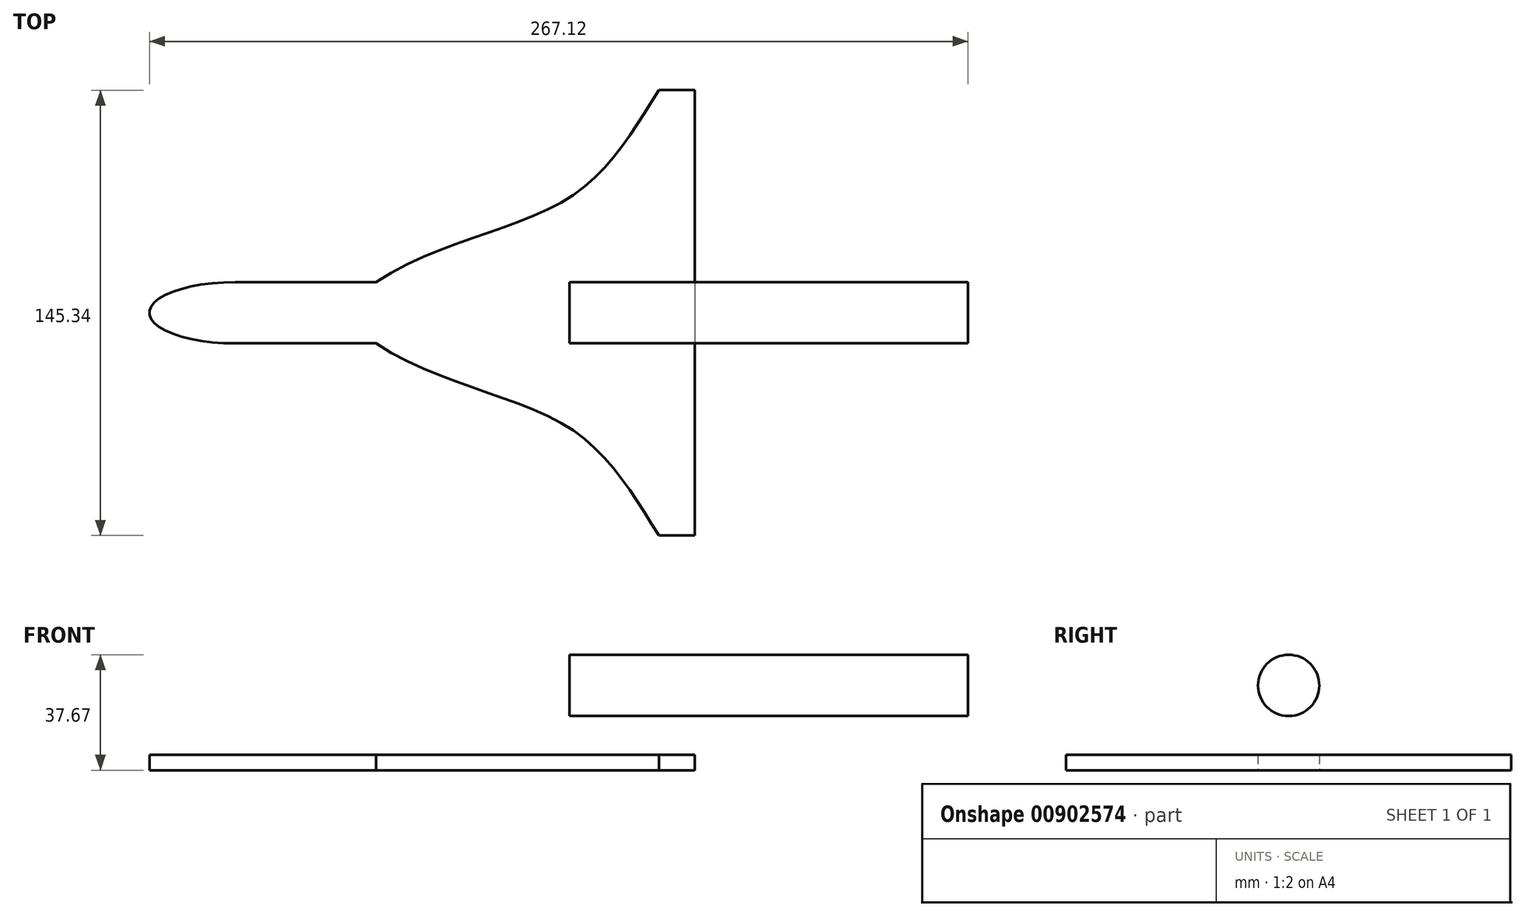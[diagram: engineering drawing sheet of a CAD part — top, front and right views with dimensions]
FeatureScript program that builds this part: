
annotation { "Feature Type Name" : "Feature", "Feature Type Description" : "" }
export const myFeature = defineFeature(function(context is Context, id is Id, definition is map)
    precondition{}
    {
        {
            var Q0;
            Q0=qCreatedBy(makeId("Top.planeOp"),FACE);
            var sketch = newSketch(context, id + "F0", { "sketchPlane" : qUnion([Q0])});
            skLineSegment(sketch, "E0", {"start": v(-109.12, 10) * mm, "end": v(40.88, 10) * mm});
            skLineSegment(sketch, "E1", {"start": v(40.88, 10) * mm, "end": v(40.88, 0) * mm});
            skLineSegment(sketch, "E2.MirrorCS", {"start": v(-109.12, -10) * mm, "end": v(40.88, -10) * mm});
            skLineSegment(sketch, "E3.MirrorCS", {"start": v(40.88, -10) * mm, "end": v(40.88, 0) * mm});
            skFitSpline(sketch, "E4", {"points": [v(-63.22, 10) * mm, v(0, 37.65) * mm, v(29.12, 72.67) * mm], "startDerivative": vector(113.66, 74.72) * mm, "endDerivative": vector(53.85, 84.54) * mm});
            skLineSegment(sketch, "E5", {"start": v(29.12, 72.67) * mm, "end": v(46, 72.67) * mm});
            skLineSegment(sketch, "E6", {"start": v(40.88, 10) * mm, "end": v(40.88, 74.12) * mm});
            skFitSpline(sketch, "E7.MirrorCS", {"points": [v(-63.22, -10) * mm, v(0, -37.65) * mm, v(29.12, -72.67) * mm], "startDerivative": vector(113.66, -74.72) * mm, "endDerivative": vector(53.85, -84.54) * mm});
            skLineSegment(sketch, "E8.MirrorCS", {"start": v(40.88, -10) * mm, "end": v(40.88, -74.12) * mm});
            skLineSegment(sketch, "E9.MirrorCS", {"start": v(29.12, -72.67) * mm, "end": v(46, -72.67) * mm});
            skLineSegment(sketch, "E10", {"start": v(-167.37, 156.75) * mm, "end": v(150, 156.75) * mm});
            skEllipse(sketch, "E11", {"center": v(-109.12, 0) * mm, "majorRadius": 28 * mm, "minorRadius": 10 * mm, "majorAxis": v(1, 0)});
            skEllipse(sketch, "E12.MirrorC", {"center": v(-112.6, 61.06) * mm, "majorRadius": 27.57 * mm, "minorRadius": 9.78 * mm, "majorAxis": v(1, 0)});
            skLineSegment(sketch, "E13", {"start": v(-112.6, 61.06) * mm, "end": v(-112.6, 86.86) * mm});
            skLineSegment(sketch, "E14", {"start": v(-154.94, 0) * mm, "end": v(-68.2, 0) * mm});
            skPoint(sketch, "E14.endSnap0", {"position": v(-81.12, 0) * mm});
            skSolve(sketch);
        }
        {
            var Q0;
            {var subQ3=sQuery(id+"F0.wireOp",EDGE,"E7.MirrorCS");Q0=makeQuery(id+"F0.imprint","IMPRINT",FACE,{"disambiguationData":[TD([[makeQuery(id+"F0.imprint","IMPRINT",EDGE,{"derivedFrom":subQ3}),1.0]])]});}
            var Q1;
            {var subQ0=sQuery(id+"F0.wireOp",EDGE,"XnzuH7Vc-KZAe-Tt8L-BqwG-Me8yOaZcINRW");var subQ1=makeQuery(id+"F0.imprint","INTERSECT",VERTEX,{"derivedFrom":[subQ0,sQuery(id+"F0.wireOp",EDGE,"E0")]});Q1=makeQuery(id+"F0.imprint","IMPRINT",FACE,{"disambiguationData":[TD([[makeQuery(id+"F0.imprint","IMPRINT",EDGE,{"disambiguationData":[TD([[subQ1,-1.0]])],"derivedFrom":subQ0}),1.0]])]});}
            var Q2;
            {var subQ0=sQuery(id+"F0.wireOp",EDGE,"E1");Q2=makeQuery(id+"F0.imprint","IMPRINT",FACE,{"disambiguationData":[TD([[makeQuery(id+"F0.imprint","IMPRINT",EDGE,{"derivedFrom":subQ0}),-1.0]])]});}
            var Q3;
            {var subQ3=sQuery(id+"F0.wireOp",EDGE,"E4");Q3=makeQuery(id+"F0.imprint","IMPRINT",FACE,{"disambiguationData":[TD([[makeQuery(id+"F0.imprint","IMPRINT",EDGE,{"derivedFrom":subQ3}),-1.0]])]});}
            var Q4;
            {var subQ0=sQuery(id+"F0.wireOp",EDGE,"MA49kEu5-NfIm-I9hH-Z6si-O17riWDiPkXM");var subQ1=makeQuery(id+"F0.imprint","INTERSECT",VERTEX,{"derivedFrom":[sQuery(id+"F0.wireOp",EDGE,"E0"),subQ0]});Q4=makeQuery(id+"F0.imprint","IMPRINT",FACE,{"disambiguationData":[TD([[makeQuery(id+"F0.imprint","IMPRINT",EDGE,{"disambiguationData":[TD([[subQ1,-1.0]])],"derivedFrom":subQ0}),1.0]])]});}
            var Q5;
            {var subQ0=sQuery(id+"F0.wireOp",EDGE,"E11");var subQ1=makeQuery(id+"F0.imprint","INTERSECT",VERTEX,{"derivedFrom":[sQuery(id+"F0.wireOp",EDGE,"E0"),subQ0]});Q5=makeQuery(id+"F0.imprint","IMPRINT",FACE,{"disambiguationData":[TD([[makeQuery(id+"F0.imprint","IMPRINT",EDGE,{"disambiguationData":[TD([[subQ1,-1.0]])],"derivedFrom":subQ0}),1.0]])]});}
            var Q6;
            {var subQ0=sQuery(id+"F0.wireOp",EDGE,"E11");var subQ1=makeQuery(id+"F0.imprint","INTERSECT",VERTEX,{"derivedFrom":[sQuery(id+"F0.wireOp",EDGE,"E2.MirrorCS"),subQ0]});Q6=makeQuery(id+"F0.imprint","IMPRINT",FACE,{"disambiguationData":[TD([[makeQuery(id+"F0.imprint","IMPRINT",EDGE,{"disambiguationData":[TD([[subQ1,1.0]])],"derivedFrom":subQ0}),1.0]])]});}
            extrude(context, id + "F1", {"entities" : qUnion([Q0, Q1, Q2, Q3, Q4, Q5, Q6]), "depth" : 5 * mm, "offsetDistance" : 25 * mm});
        }
        {
            var Q0;
            Q0=qCreatedBy(makeId("Right.planeOp"),FACE);
            var sketch = newSketch(context, id + "F2", { "sketchPlane" : qUnion([Q0])});
            skCircle(sketch, "E15", {"center": v(0, 27.67) * mm, "radius": 10 * mm});
            skLineSegment(sketch, "E16", {"start": v(10, 27.67) * mm, "end": v(9.91, 11.67) * mm});
            skLineSegment(sketch, "E17", {"start": v(9.91, 11.67) * mm, "end": v(-10.09, 11.67) * mm});
            skLineSegment(sketch, "E18", {"start": v(-10.09, 11.67) * mm, "end": v(-10, 27.57) * mm});
            skSolve(sketch);
        }
        {
            var Q0;
            {var subQ0=sQuery(id+"F2.wireOp",EDGE,"E16");Q0=makeQuery(id+"F2.imprint","IMPRINT",FACE,{"disambiguationData":[TD([[makeQuery(id+"F2.imprint","IMPRINT",EDGE,{"derivedFrom":subQ0}),-1.0]])]});}
            var Q1;
            {var subQ0=sQuery(id+"F2.wireOp",EDGE,"E15");var subQ1=makeQuery(id+"F2.imprint","INTERSECT",VERTEX,{"derivedFrom":[subQ0,sQuery(id+"F2.wireOp",EDGE,"E16")]});Q1=makeQuery(id+"F2.imprint","IMPRINT",FACE,{"disambiguationData":[TD([[makeQuery(id+"F2.imprint","IMPRINT",EDGE,{"disambiguationData":[TD([[subQ1,1.0]])],"derivedFrom":subQ0}),1.0]])]});}
            extrude(context, id + "F3", {"entities" : qUnion([Q0, Q1]), "depth" : 130 * mm, "offsetDistance" : 25 * mm});
        }
    });
